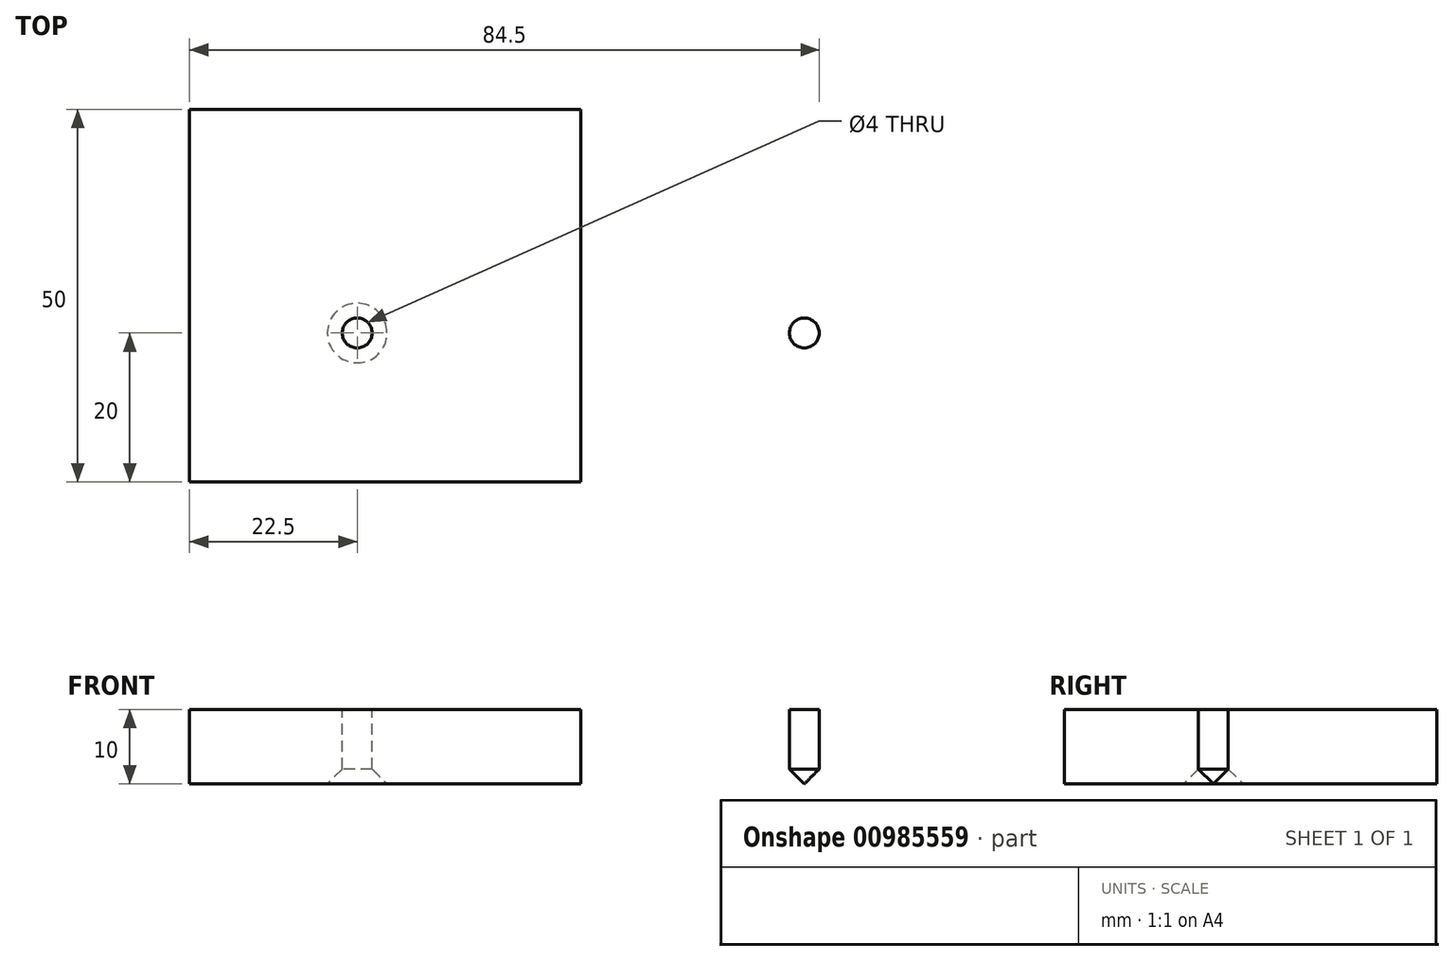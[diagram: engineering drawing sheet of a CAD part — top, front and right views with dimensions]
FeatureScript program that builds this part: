
annotation { "Feature Type Name" : "Feature", "Feature Type Description" : "" }
export const myFeature = defineFeature(function(context is Context, id is Id, definition is map)
    precondition{}
    {
        {
            var Q0;
            Q0=qCreatedBy(makeId("Top.planeOp"),FACE);
            var sketch = newSketch(context, id + "F0", { "sketchPlane" : qUnion([Q0])});
            skLineSegment(sketch, "E0.bottom", {"start": v(52.5, -25) * mm, "end": v(-52.5, -25) * mm});
            skLineSegment(sketch, "E0.top", {"start": v(52.5, 25) * mm, "end": v(-52.5, 25) * mm});
            skLineSegment(sketch, "E0.left", {"start": v(52.5, -25) * mm, "end": v(52.5, 25) * mm});
            skLineSegment(sketch, "E0.right", {"start": v(-52.5, -25) * mm, "end": v(-52.5, 25) * mm});
            skPoint(sketch, "E0.middle", {"position": v(0, 0) * mm});
            skSolve(sketch);
        }
        {
            var Q0;
            Q0 = qSketchRegion(id + "F0", true);
            extrude(context, id + "F1", {"entities" : qUnion([Q0]), "depth" : 10 * mm, "offsetDistance" : 25.4 * mm});
        }
        {
            var Q0;
            Q0=makeQuery(id+"F1.opExtrude","CAP_FACE",FACE,{"disambiguationData":[OSD([sQuery(id+"F0.wireOp",EDGE,"E0.bottom"),sQuery(id+"F0.wireOp",EDGE,"E0.top"),sQuery(id+"F0.wireOp",EDGE,"E0.left"),sQuery(id+"F0.wireOp",EDGE,"E0.right")])],"isStart":false});
            var sketch = newSketch(context, id + "F2", { "sketchPlane" : qUnion([Q0])});
            skLineSegment(sketch, "E1", {"start": v(-110.48, -5) * mm, "end": v(115.3, -5) * mm});
            skLineSegment(sketch, "E2", {"start": v(0, 43.44) * mm, "end": v(0, -52.95) * mm});
            skPoint(sketch, "E2.startSnap0", {"position": v(0, 25) * mm});
            skPoint(sketch, "E2.endSnap0", {"position": v(0, -25) * mm});
            skCircle(sketch, "E3", {"center": v(-30, -5) * mm, "radius": 2 * mm});
            skCircle(sketch, "E4", {"center": v(30, -5) * mm, "radius": 2 * mm});
            skSolve(sketch);
        }
        {
            var Q0;
            {var subQ0=sQuery(id+"F2.wireOp",EDGE,"E3");var subQ1=sQuery(id+"F2.wireOp",EDGE,"E1");var subQ2=makeQuery(id+"F2.imprint","INTERSECT",VERTEX,{"disambiguationData":[OD(0.0)],"derivedFrom":[subQ1,subQ0]});Q0=makeQuery(id+"F2.imprint","IMPRINT",FACE,{"disambiguationData":[TD([[makeQuery(id+"F2.imprint","IMPRINT",EDGE,{"disambiguationData":[TD([[subQ2,-1.0]])],"derivedFrom":subQ1}),1.0]])]});}
            var Q1;
            {var subQ0=sQuery(id+"F2.wireOp",EDGE,"E3");var subQ1=sQuery(id+"F2.wireOp",EDGE,"E1");var subQ2=makeQuery(id+"F2.imprint","INTERSECT",VERTEX,{"disambiguationData":[OD(0.0)],"derivedFrom":[subQ1,subQ0]});Q1=makeQuery(id+"F2.imprint","IMPRINT",FACE,{"disambiguationData":[TD([[makeQuery(id+"F2.imprint","IMPRINT",EDGE,{"disambiguationData":[TD([[subQ2,-1.0]])],"derivedFrom":subQ1}),-1.0]])]});}
            var Q2;
            {var subQ0=sQuery(id+"F2.wireOp",EDGE,"E4");var subQ1=sQuery(id+"F2.wireOp",EDGE,"E1");var subQ2=makeQuery(id+"F2.imprint","INTERSECT",VERTEX,{"disambiguationData":[OD(0.0)],"derivedFrom":[subQ1,subQ0]});Q2=makeQuery(id+"F2.imprint","IMPRINT",FACE,{"disambiguationData":[TD([[makeQuery(id+"F2.imprint","IMPRINT",EDGE,{"disambiguationData":[TD([[subQ2,-1.0]])],"derivedFrom":subQ1}),1.0]])]});}
            var Q3;
            {var subQ0=sQuery(id+"F2.wireOp",EDGE,"E4");var subQ1=sQuery(id+"F2.wireOp",EDGE,"E1");var subQ2=makeQuery(id+"F2.imprint","INTERSECT",VERTEX,{"disambiguationData":[OD(0.0)],"derivedFrom":[subQ1,subQ0]});Q3=makeQuery(id+"F2.imprint","IMPRINT",FACE,{"disambiguationData":[TD([[makeQuery(id+"F2.imprint","IMPRINT",EDGE,{"disambiguationData":[TD([[subQ2,-1.0]])],"derivedFrom":subQ1}),-1.0]])]});}
            extrude(context, id + "F3", {"entities" : qUnion([Q0, Q1, Q2, Q3]), "operationType" : NewBodyOperationType.REMOVE, "endBound" : BoundingType.THROUGH_ALL, "oppositeDirection" : true, "depth" : 25.4 * mm, "offsetDistance" : 25.4 * mm});
        }
        {
            var Q0;
            Q0=makeQuery(id+"F3.boolean.opBoolean","INTERSECT",EDGE,{"derivedFrom":[makeQuery(id+"F1.opExtrude","CAP_FACE",FACE,{"disambiguationData":[OSD([sQuery(id+"F0.wireOp",EDGE,"E0.bottom"),sQuery(id+"F0.wireOp",EDGE,"E0.top"),sQuery(id+"F0.wireOp",EDGE,"E0.left"),sQuery(id+"F0.wireOp",EDGE,"E0.right")])],"isStart":true}),makeQuery(id+"F3.opExtrude","SWEPT_FACE",FACE,{"disambiguationData":[OSD([sQuery(id+"F2.wireOp",EDGE,"E4")])]})]});
            var Q1;
            Q1=makeQuery(id+"F3.boolean.opBoolean","INTERSECT",EDGE,{"derivedFrom":[makeQuery(id+"F1.opExtrude","CAP_FACE",FACE,{"disambiguationData":[OSD([sQuery(id+"F0.wireOp",EDGE,"E0.bottom"),sQuery(id+"F0.wireOp",EDGE,"E0.top"),sQuery(id+"F0.wireOp",EDGE,"E0.left"),sQuery(id+"F0.wireOp",EDGE,"E0.right")])],"isStart":true}),makeQuery(id+"F3.opExtrude","SWEPT_FACE",FACE,{"disambiguationData":[OSD([sQuery(id+"F2.wireOp",EDGE,"E3")])]})]});
            chamfer(context, id + "F4", {"entities" : qUnion([Q0, Q1]), "width" : 2 * mm, "tangentPropagation" : true});
        }
    });
